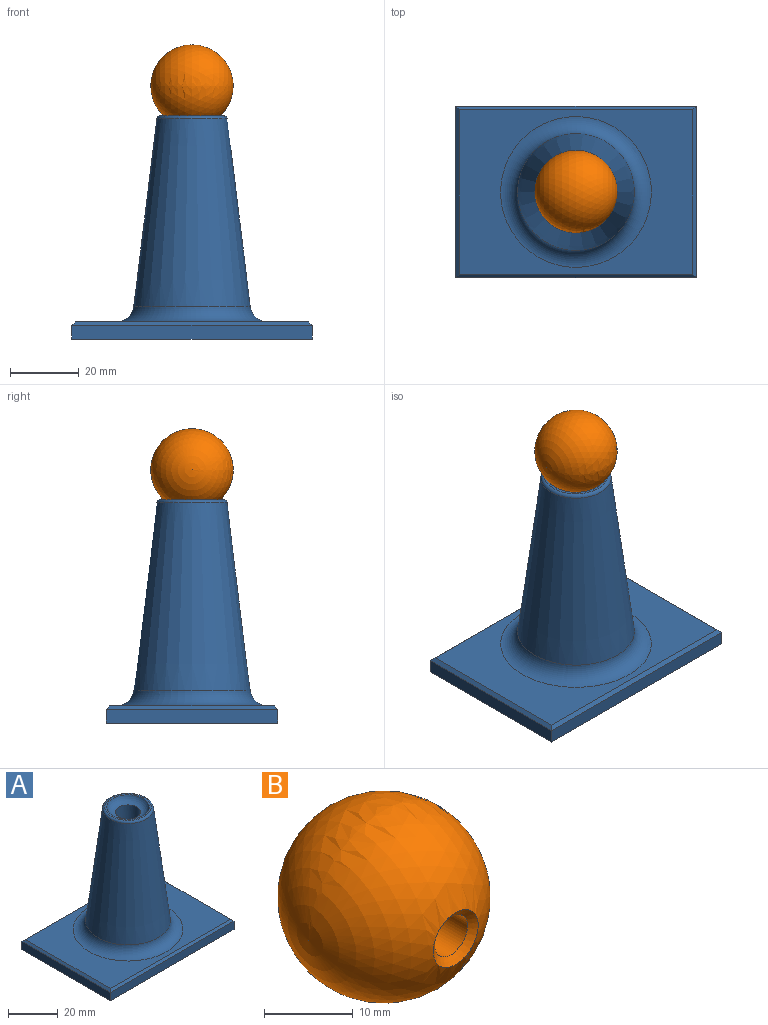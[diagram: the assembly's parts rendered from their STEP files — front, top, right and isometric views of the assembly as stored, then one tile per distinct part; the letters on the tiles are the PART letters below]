
ASSEMBLY  parts=2 mates=1
PART A: 20 faces, bbox 70.3x55.4x66.8 mm
  f0: plane 7.81x7.81mm, normal (0,0,-1), area 19.6mm2, adj f1,f2
  f1: cylinder r=3.9mm len=50.5mm, axis (0,0,-1), area 1238.6mm2, adj f0,f3
  f2: cylinder r=3mm len=6mm, axis (0,0,-1), area 94.2mm2, adj f0,f4
  f3: plane 70x50mm, normal (0,0,-1), area 3452.1mm2, adj f1,f5,f6,f7,f8
  f4: plane 10x10mm, normal (0,0,1), area 50.3mm2, adj f2,f9
  f5: plane 50x4mm, normal (1,0,0), area 200mm2, adj f3,f6,f8,f10
  f6: plane 70x4mm, normal (0,1,0), area 280mm2, adj f3,f5,f7,f11
  f7: plane 50x4mm, normal (-1,0,0), area 200mm2, adj f3,f6,f8,f12
  f8: plane 70x4mm, normal (0,-1,0), area 280mm2, adj f3,f5,f7,f13
  f9: cylinder r=5mm len=10mm, axis (0,0,-1), area 219.9mm2, adj f4,f14
  f10: plane 50x1mm, normal (0.71,0,0.71), area 69.3mm2, adj f5,f11,f13,f15
  f11: plane 70x1mm, normal (0,0.71,0.71), area 97.6mm2, adj f6,f10,f12,f15
  f12: plane 50x1mm, normal (-0.71,0,0.71), area 69.3mm2, adj f7,f11,f13,f15
  f13: plane 70x1mm, normal (0,-0.71,0.71), area 97.6mm2, adj f8,f10,f12,f15
  f14: torus R=4.79mm, axis (0,0,-1), area 199.5mm2, adj f9,f16
  f15: plane 68x48mm, normal (0,0,1), area 1755mm2, adj f10,f11,f12,f13,f17
  f16: plane 18.77x18.77mm, normal (0,0,1), area 41.5mm2, adj f14,f18
  f17: torus R=21.92mm, axis (0,0,-1), area 859.8mm2, adj f15,f19
  f18: torus R=9.25mm, axis (0,0,-1), area 89.7mm2, adj f16,f19
  f19: cone r=16.96mm half-angle=7deg, axis (0,0,-1), area 4712.3mm2, adj f17,f18
PART B: 4 faces, bbox 24x24x24 mm
  f0: plane 5.25x5.25mm, normal (0,-1,0), area 21.6mm2, adj f1
  f1: cylinder r=2.62mm len=10.71mm, axis (0,-1,0), area 176.6mm2, adj f0,f2
  f2: cone r=3.59mm half-angle=52.5deg, axis (0,-1,0), area 23.8mm2, adj f1,f3
  f3: sphere r=12mm, area 1768.1mm2, adj f2
PLACE A t=(-3.05,0.4,0)mm
PLACE B rot(axis=(1,0,0),90deg) t=(-3.05,0.4,73.68)mm
MATE cylindrical B.f1 <-> A.f1  axis (0,0,-1) through (-3.05,0.4,68.32)mm
